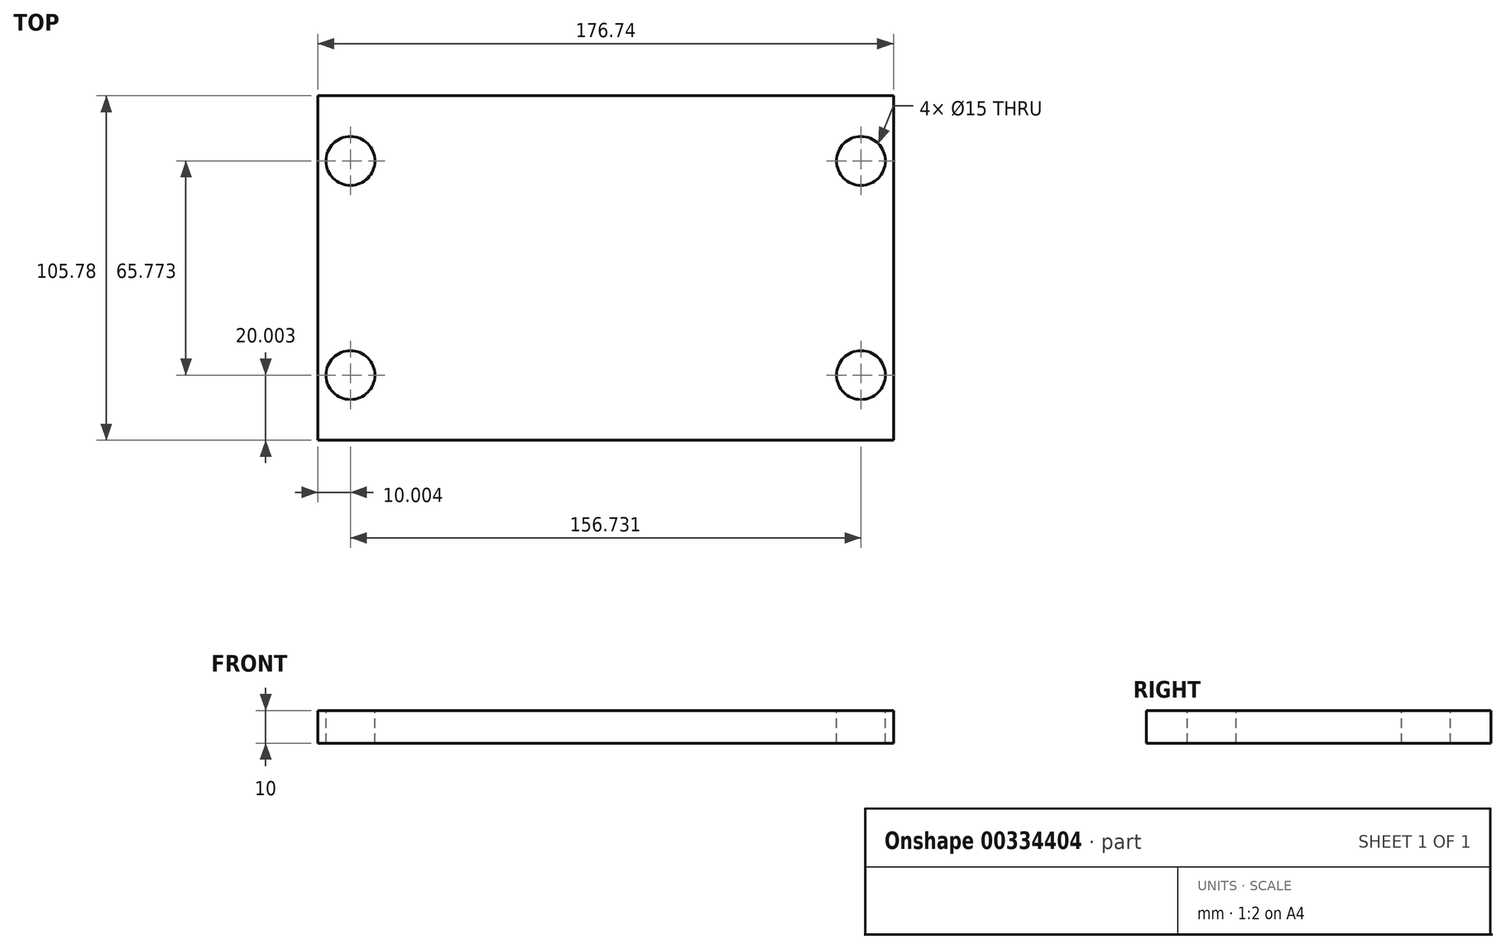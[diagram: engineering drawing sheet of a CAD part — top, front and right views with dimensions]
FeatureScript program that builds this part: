
annotation { "Feature Type Name" : "Feature", "Feature Type Description" : "" }
export const myFeature = defineFeature(function(context is Context, id is Id, definition is map)
    precondition{}
    {
        {
            var Q0;
            Q0=qCreatedBy(makeId("Top.planeOp"),FACE);
            var sketch = newSketch(context, id + "F0", { "sketchPlane" : qUnion([Q0])});
            skLineSegment(sketch, "E0.bottom", {"start": v(88.37, -52.89) * mm, "end": v(-88.37, -52.89) * mm});
            skLineSegment(sketch, "E0.top", {"start": v(88.37, 52.89) * mm, "end": v(-88.37, 52.89) * mm});
            skLineSegment(sketch, "E0.left", {"start": v(88.37, -52.89) * mm, "end": v(88.37, 52.89) * mm});
            skLineSegment(sketch, "E0.right", {"start": v(-88.37, -52.89) * mm, "end": v(-88.37, 52.89) * mm});
            skPoint(sketch, "E0.middle", {"position": v(0, 0) * mm});
            skSolve(sketch);
        }
        {
            var Q0;
            Q0 = qSketchRegion(id + "F0", true);
            extrude(context, id + "F1", {"entities" : qUnion([Q0]), "depth" : 10 * mm});
        }
        {
            var Q0;
            Q0=makeQuery(id+"F1.opExtrude","CAP_FACE",FACE,{"disambiguationData":[OSD([sQuery(id+"F0.wireOp",EDGE,"E0.bottom"),sQuery(id+"F0.wireOp",EDGE,"E0.top"),sQuery(id+"F0.wireOp",EDGE,"E0.left"),sQuery(id+"F0.wireOp",EDGE,"E0.right")])],"isStart":false});
            var sketch = newSketch(context, id + "F2", { "sketchPlane" : qUnion([Q0])});
            skCircle(sketch, "E1", {"center": v(-78.37, 32.89) * mm, "radius": 7.5 * mm});
            skCircle(sketch, "E2", {"center": v(78.37, 32.89) * mm, "radius": 7.5 * mm});
            skCircle(sketch, "E3", {"center": v(-78.37, -32.89) * mm, "radius": 7.5 * mm});
            skCircle(sketch, "E4", {"center": v(78.37, -32.89) * mm, "radius": 7.5 * mm});
            skSolve(sketch);
        }
        {
            var Q0;
            Q0=makeQuery(id+"F2.imprint","IMPRINT",FACE,{"disambiguationData":[TD([[makeQuery(id+"F2.imprint","IMPRINT",EDGE,{"derivedFrom":sQuery(id+"F2.wireOp",EDGE,"E1")}),1.0]])]});
            var Q1;
            Q1=makeQuery(id+"F2.imprint","IMPRINT",FACE,{"disambiguationData":[TD([[makeQuery(id+"F2.imprint","IMPRINT",EDGE,{"derivedFrom":sQuery(id+"F2.wireOp",EDGE,"E3")}),1.0]])]});
            var Q2;
            Q2=makeQuery(id+"F2.imprint","IMPRINT",FACE,{"disambiguationData":[TD([[makeQuery(id+"F2.imprint","IMPRINT",EDGE,{"derivedFrom":sQuery(id+"F2.wireOp",EDGE,"E2")}),1.0]])]});
            var Q3;
            Q3=makeQuery(id+"F2.imprint","IMPRINT",FACE,{"disambiguationData":[TD([[makeQuery(id+"F2.imprint","IMPRINT",EDGE,{"derivedFrom":sQuery(id+"F2.wireOp",EDGE,"E4")}),1.0]])]});
            extrude(context, id + "F3", {"entities" : qUnion([Q0, Q1, Q2, Q3]), "operationType" : NewBodyOperationType.REMOVE, "endBound" : BoundingType.THROUGH_ALL, "oppositeDirection" : true, "depth" : 25 * mm});
        }
    });
